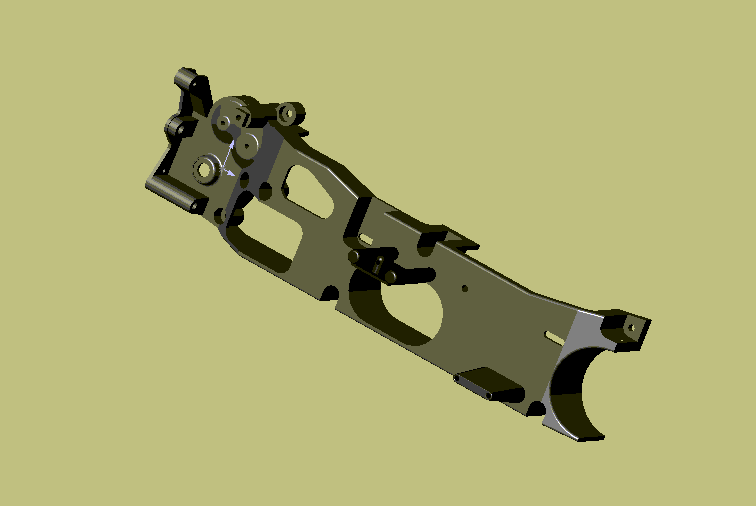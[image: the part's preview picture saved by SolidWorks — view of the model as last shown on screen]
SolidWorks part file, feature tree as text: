
SOLIDWORKS PART (.sldprt)
format: sldprt  version: not decoded by parser v0  size: 1,341,952 bytes
history: native  units: mm
features: sketch x74, cut_extrude x43, extrude x26, fillet x7, plane x6, material x1, shell x1 (+8 scaffold rows collapsed)
feature tree (166):
  scaffold x8  (default folders/planes/origin — collapsed)
  material  "Matériau <non spécifié>"
  plane  "Plane1"
  plane  "Plane2"
  plane  "Plane3"
  sketch  "Esquisse1"  dims[c1.D6=40.0mm c1.D9=6.0mm c1.D4=~4.910474mm c1.D11=28.0mm c1.D13=6.0mm c1.D3=10.0mm c1.D18=10.0mm c1.D19=14.0mm c2.D11=28.0mm c2.D15=14.0mm c3.D11=30.0mm c3.D15=1.0mm c4.D11=22.0mm c4.D21=2.0mm c4.D9=2.0mm c4.D10=3.0mm c5.D9=6.0mm c5.D2=18.0mm c5.D5=6.0mm c5.D6=24.0mm c5.D1=38.0mm c6.D2=~19.312574mm c6.D1=20.0mm c7.D2=38.0mm c7.D3=35.0mm c7.D4=18.0mm c7.D5=18.0mm c7.D7=12.0mm c7.D8=17.0mm c8.D4=23.0mm c8.D6=21.0mm c9.D4=6.0mm c9.D7=14.0mm c9.D8=25.0mm c9.D10=15.0mm c9.D12=16.0mm c9.D14=22.0mm c9.D15=15.0mm c9.D16=23.0mm c9.D17=8.0mm c9.D19=5.0mm c9.D20=30.0mm c9.D21=23.0mm c10.D14=18.0mm c10.D20=23.0mm c10.D21=16.0mm c10.D10=16.0mm c10.D22=14.0mm c10.D1=23.0mm c10.D2=25.0mm c10.D3=15.0mm c10.D4=~1.474586mm c10.D5=20.0mm c10.D6=5.0mm c10.D7=14.0mm c10.D8=16.0mm c11.D5=20.5mm c11.D9=~21.260292mm c11.D8=2.0mm c12.D9=2.0mm c12.D10=2.0mm c12.D11=0.5mm c12.D1=2.0mm]
  sketch  "Esquisse2"  dims[c1.D8=7.0mm c1.D1=18.0mm c1.D2=12.0mm c2.D1=8.0mm c2.D2=4.0mm c2.D3=14.0mm c2.D4=130.0mm c2.D5=22.0mm c2.D6=174.5mm c2.D7=22.0mm]
  sketch  "Esquisse3"  dims[D1=45.0mm D2=12.0mm D3=22.0mm D4=18.0mm D5=15.0mm D6=40.0mm D7=20.0mm D8=35.0mm]
  sketch  "Esquisse4"  dims[D1=5.0mm D2=~135.966117mm]
  sketch  "Esquisse5"  dims[c1.D2=36.0mm c1.D1=34.0mm c1.D5=24.0mm c1.D6=17.0mm c1.D7=12.0mm c1.D10=16.5mm c1.D11=~11.949177mm c2.D1=222.0mm c2.D3=27.0mm c3.D1=217.0mm c3.D3=228.0mm c4.D1=22.8mm c4.D4=19.0mm c5.D1=22.8mm c5.D4=13.0mm c5.D5=14.0mm c5.D6=18.0mm c5.D8=30.0mm c5.D9=2.0mm c5.D2=2.0mm c6.D9=~17.995555mm c6.D6=~17.995555mm c6.D5=19.25mm c7.D6=18.0mm c7.D9=21.0mm]
  sketch  "Esquisse7"  dims[c1.D1=4.0mm c1.D2=2.0mm c1.D3=~18.326793mm c2.D1=194.03mm]
  extrude  "Base-Extrusion"  Depth=27mm
  sketch  "Esquisse8"  dims[c1.D1=12.0mm c1.D2=33.0mm c1.D3=54.0mm c1.D4=159.5mm c1.D5=22.0mm c1.D6=22.0mm c2.D5=5.0mm]
  cut_extrude  "Enlèv. mat.-Extru.1"  Depth=87mm
  sketch  "Esquisse9"
  cut_extrude  "Enlèv. mat.-Extru.2"  [1 undecoded]
  sketch  "Esquisse10"  dims[c1.D1=40.0mm c1.D3=40.0mm c2.D1=40.0mm c2.D2=42.0mm c3.D1=40.0mm c3.D2=53.0mm c4.D1=3.0mm]
  cut_extrude  "Enlèv. mat.-Extru.3"  [1 undecoded]
  sketch  "Esquisse11"  dims[c1.D1=14.0mm c1.D2=20.0mm c1.D4=100.0mm c2.D1=122.0mm c2.D3=2.0mm]
  cut_extrude  "Enlèv. mat.-Extru.8"  [1 undecoded]
  sketch  "Esquisse12"  dims[D4=4.0mm D1=14.0mm D2=21.0mm D3=97.0mm]
  shell  "Coque14"  Thickness=2mm
  sketch  "Esquisse16"  dims[c1.D1=3.0mm c1.D2=3.0mm c2.D1=5.0mm c2.D3=3.0mm c2.D2=3.0mm c2.D5=3.0mm c2.D6=5.0mm c3.D2=8.0mm c3.D3=6.0mm c3.D4=32.0mm]
  cut_extrude  "Enlèv. mat.-Extru.11"  [1 undecoded]
  sketch  "Esquisse17"  dims[c1.D3=4.0mm c1.D1=1.5mm c1.D2=1.5mm c2.D3=~0.877384mm]
  extrude  "Boss.-Extru.8"  Depth=13.5mm
  cut_extrude  "Enlèv. mat.-Extru.12"  Depth=12mm
  sketch  "Esquisse18"  dims[D1=18.0mm D2=3.0mm D3=8.0mm]
  cut_extrude  "Enlèv. mat.-Extru.13"  [1 undecoded]
  sketch  "Esquisse19"  dims[c1.D6=40.0mm c1.D9=6.0mm c1.D4=~4.910474mm c1.D11=28.0mm c1.D13=6.0mm c1.D3=10.0mm c1.D18=10.0mm c1.D19=14.0mm c2.D11=28.0mm c2.D15=14.0mm c3.D11=30.0mm c3.D15=1.0mm c4.D11=22.0mm c4.D21=2.0mm c4.D9=2.0mm c4.D10=3.0mm c5.D9=6.0mm c5.D2=18.0mm c5.D5=6.0mm c5.D6=24.0mm c5.D4=12.0mm c5.D1=20.0mm c6.D2=38.0mm c6.D3=35.0mm c6.D4=18.0mm c6.D5=18.0mm c6.D7=12.0mm c6.D8=17.0mm c7.D4=23.0mm c7.D6=21.0mm c8.D4=6.0mm c8.D7=14.0mm c8.D8=25.0mm c8.D10=15.0mm c8.D12=16.0mm c8.D14=22.0mm c8.D15=15.0mm c8.D16=23.0mm c8.D17=8.0mm c8.D19=5.0mm c8.D20=30.0mm c8.D21=23.0mm c9.D14=18.0mm c9.D20=23.0mm c9.D21=16.0mm c9.D10=16.0mm c9.D22=14.0mm c9.D1=23.0mm c9.D2=25.0mm c9.D3=15.0mm c9.D4=~1.474586mm c9.D5=20.0mm c9.D6=5.0mm c9.D7=14.0mm c9.D8=16.0mm c10.D5=20.5mm c10.D9=~21.260292mm c10.D8=2.0mm c11.D9=2.0mm c11.D10=2.0mm c11.D11=0.5mm c11.D1=2.0mm c11.D2=15.2mm c11.D3=23.2mm c11.D5=~34.247688mm c11.D6=19.25mm]
  extrude  "Boss.-Extru.9"  [1 undecoded]
  sketch  "Esquisse20"
  cut_extrude  "Enlèv. mat.-Extru.14"  [1 undecoded]
  sketch  "Esquisse21"  dims[D1=27.0mm]
  extrude  "Boss.-Extru.10"  Depth=8mm
  sketch  "Esquisse22"
  sketch  "Esquisse24"  dims[D1=2.0mm D2=2.0mm]
  sketch  "Esquisse25"
  extrude  "Boss.-Extru.12"  Depth=8mm
  cut_extrude  "Enlèv. mat.-Extru.17"  Depth=6mm
  sketch  "Esquisse26"
  cut_extrude  "Enlèv. mat.-Extru.18"  Depth=6mm
  sketch  "Esquisse27"  dims[D1=5.0mm D2=9.0mm D3=9.0mm D4=5.0mm]
  sketch  "Esquisse29"  dims[D1=13.0mm]
  extrude  "Boss.-Extru.14"  Depth=4mm
  sketch  "Esquisse30"  dims[D1=11.0mm]
  cut_extrude  "Enlèv. mat.-Extru.19"  Depth=4mm
  sketch  "Esquisse31"  dims[D1=6.0mm]
  cut_extrude  "Enlèv. mat.-Extru.20"  [1 undecoded]
  sketch  "Esquisse32"  dims[D1=10.0mm]
  cut_extrude  "Enlèv. mat.-Extru.21"  Depth=0.5mm
  fillet  "Congé1"  Radius=1mm
  cut_extrude  "Enlèv. mat.-Extru.22"  [1 undecoded]
  sketch  "Esquisse33"  dims[c1.D5=8.0mm c1.D6=2.0mm c1.D4=3.5mm c1.D9=4.5mm c1.D13=2.0mm c1.D16=2.0mm c1.D20=4.0mm c1.D1=27.0mm c1.D2=23.0mm c1.D3=23.0mm c2.D4=32.0mm c2.D1=~1.086371mm c2.D2=~4.577798mm c2.D3=~6.268805mm c2.D5=~20.368425mm c2.D6=~22.368425mm c2.D7=~5.486411mm c2.D8=~3.722962mm c2.D10=~4.480709mm c2.D11=~2.79739mm c2.D12=~1.991426mm c2.D14=~8.25742mm c2.D15=~7.451456mm c2.D17=~1.864614mm c2.D18=~2.575873mm c2.D19=~3.829958mm c2.D21=~3.95603mm c2.D22=~0.95603mm c2.D23=~19.561627mm c2.D24=~8.593709mm c2.D25=~10.24482mm c2.D26=7.0mm c2.D27=7.0mm c2.D28=~14.527757mm c2.D29=~14.406696mm c2.D30=~22.153872mm c2.D31=12.0mm c2.D32=12.0mm c2.D33=38.0mm]
  extrude  "Boss.-Extru.16"  Depth=1.5mm
  sketch  "Esquisse35"
  extrude  "Boss.-Extru.17"  Depth=22.5mm
  sketch  "Esquisse36"  dims[D1=8.0mm]
  extrude  "Boss.-Extru.18"  Depth=4mm
  sketch  "Esquisse37"  dims[c1.D6=4.0mm c1.D1=~8.352254mm c1.D2=~4.379415mm c1.D3=~3.829958mm c1.D4=~1.153872mm c1.D5=~0.436764mm c2.D6=~9.881926mm c2.D7=~10.474589mm c2.D8=16.56mm c2.D9=21.0mm]
  extrude  "Boss.-Extru.19"  Depth=5mm
  sketch  "Esquisse38"  dims[D1=~4.01424mm]
  extrude  "Boss.-Extru.20"  Depth=1.5mm
  sketch  "Esquisse39"  dims[D1=2.0mm D2=4.0mm D3=3.0mm]
  cut_extrude  "Enlèv. mat.-Extru.23"  [1 undecoded]
  fillet  "Congé2"  Radius=1mm
  fillet  "Congé3"  Radius=1mm
  sketch  "Esquisse42"  dims[c1.D4=5.0mm c1.D8=3.0mm c1.D3=3.0mm c1.D6=3.0mm c1.D11=5.0mm c1.D12=5.0mm c2.D8=5.0mm c2.D1=14.0mm c2.D2=32.0mm c2.D3=75.0mm c2.D5=20.0mm c2.D6=72.0mm c2.D7=22.0mm c3.D1=19.0mm c3.D2=66.0mm c3.D4=72.0mm c3.D5=19.0mm c3.D7=20.0mm c3.D8=14.0mm c3.D9=9.0mm c3.D10=65.0mm c3.D13=9.0mm c4.D13=90.0deg c5.D13=9.0mm c5.D14=75.0mm c5.D15=19.84mm c5.D16=27.02mm c5.D9=9.0mm c6.D9=90.0deg c7.D9=8.0mm c7.D10=8.0mm]
  cut_extrude  "Enlèv. mat.-Extru.24"  Depth=20mm
  sketch  "Esquisse43"
  cut_extrude  "Enlèv. mat.-Extru.25"  Depth=10mm
  sketch  "Esquisse46"  dims[D2=10.0mm D1=45.0mm]
  extrude  "Boss.-Extru.23"  Depth=14mm
  sketch  "Esquisse48"  dims[D1=8.0mm]
  cut_extrude  "Enlèv. mat.-Extru.27"  Depth=13mm
  sketch  "Esquisse49"  dims[D1=3.0mm]
  cut_extrude  "Enlèv. mat.-Extru.28"  [1 undecoded]
  sketch  "Esquisse50"  dims[D1=5.0mm]
  cut_extrude  "Enlèv. mat.-Extru.29"  [1 undecoded]
  sketch  "Esquisse51"  dims[c1.D2=10.0mm c1.D1=5.0mm c1.D3=10.0mm c2.D1=5.0mm]
  extrude  "Boss.-Extru.24"  [1 undecoded]
  sketch  "Esquisse54"  dims[D1=3.0mm]
  cut_extrude  "Enlèv. mat.-Extru.32"  [1 undecoded]
  sketch  "Esquisse55"  dims[D1=7.0mm]
  cut_extrude  "Enlèv. mat.-Extru.33"  Depth=4mm
  plane  "Plan1"  Offset=8mm
  sketch  "Esquisse57"
  cut_extrude  "Enlèv. mat.-Extru.35"  [1 undecoded]
  sketch  "Esquisse58"  dims[D1=3.0mm]
  cut_extrude  "Enlèv. mat.-Extru.36"  [1 undecoded]
  sketch  "Esquisse59"  dims[D1=7.0mm]
  cut_extrude  "Enlèv. mat.-Extru.37"  Depth=4mm
  sketch  "Esquisse60"  dims[D1=7.0mm]
  cut_extrude  "Enlèv. mat.-Extru.38"  Depth=3mm
  fillet  "Congé4"  Radius=1mm
  sketch  "Esquisse61"  dims[D1=10.0mm D2=17.0mm D3=16.6mm]
  cut_extrude  "Enlèv. mat.-Extru.39"  Depth=10mm
  plane  "Plan2"  Offset=11mm
  sketch  "Esquisse64"
  extrude  "Boss.-Extru.29"  [1 undecoded]
  sketch  "Esquisse65"
  cut_extrude  "Enlèv. mat.-Extru.40"  Depth=5mm
  extrude  "Boss.-Extru.30"  Depth=6mm
  sketch  "Esquisse66"
  extrude  "Boss.-Extru.31"  Depth=10mm
  sketch  "Esquisse67"
  extrude  "Boss.-Extru.32"  [1 undecoded]
  sketch  "Esquisse68"  dims[c1.D1=10.0mm c1.D2=~4.410927mm c1.D3=~4.410927mm c1.D4=10.0mm c2.D1=~37.209373mm c2.D2=5.0mm c2.D3=78.0mm c2.D5=33.0mm]
  extrude  "Boss.-Extru.33"  [1 undecoded]
  sketch  "Esquisse69"  dims[c1.D1=7.0mm c1.D2=7.0mm c2.D1=5.0mm]
  cut_extrude  "Enlèv. mat.-Extru.41"  Depth=4mm
  sketch  "Esquisse70"  dims[D1=8.0mm D2=8.0mm D3=8.0mm]
  cut_extrude  "Enlèv. mat.-Extru.44"  Depth=22mm
  sketch  "Esquisse71"  dims[D1=3.0mm D2=3.0mm]
  cut_extrude  "Enlèv. mat.-Extru.45"  [1 undecoded]
  sketch  "Esquisse72"  dims[D1=6.0mm D2=6.0mm D3=3.0mm D4=3.0mm]
  extrude  "Boss.-Extru.34"  Depth=3mm
  sketch  "Esquisse73"  dims[D1=2.5mm]
  cut_extrude  "Enlèv. mat.-Extru.46"  Depth=10mm
  sketch  "Esquisse74"  dims[D3=6.0mm D1=10.0mm D2=18.0mm]
  extrude  "Boss.-Extru.35"  Depth=32mm
  sketch  "Esquisse75"
  extrude  "Boss.-Extru.36"  Depth=1mm
  fillet  "Congé6"  Radius=1mm
  sketch  "Esquisse76"  dims[D2=4.0mm D1=10.0mm D3=5.0mm]
  extrude  "Boss.-Extru.37"  Depth=8mm
  fillet  "Congé9"  Radius=2mm
  sketch  "Esquisse77"  dims[D2=2.0mm D1=10.0mm D3=6.0mm]
  cut_extrude  "Enlèv. mat.-Extru.47"  Depth=18mm
  sketch  "Esquisse78"  dims[c1.D2=3.0mm c1.D3=3.0mm c1.D4=3.0mm c1.D8=3.0mm c1.D9=3.0mm c1.D1=12.0mm c1.D5=8.0mm c1.D6=44.0mm c1.D7=22.0mm c2.D4=7.0mm c2.D10=16.5mm c2.D11=30.0mm]
  cut_extrude  "Enlèv. mat.-Extru.48"  [1 undecoded]
  sketch  "Esquisse79"  dims[D3=10.0mm D1=93.75mm D2=7.25mm]
  extrude  "Boss.-Extru.38"  Depth=40mm
  sketch  "Esquisse80"
  cut_extrude  "Enlèv. mat.-Extru.49"  Depth=40mm
  sketch  "Esquisse81"  dims[D1=8.0mm]
  cut_extrude  "Enlèv. mat.-Extru.50"  Depth=22mm
  sketch  "Esquisse82"  dims[D1=7.0mm]
  cut_extrude  "Enlèv. mat.-Extru.51"  Depth=2mm
  sketch  "Esquisse83"  dims[D1=3.0mm]
  cut_extrude  "Enlèv. mat.-Extru.52"  [1 undecoded]
  sketch  "Esquisse84"
  cut_extrude  "Enlèv. mat.-Extru.54"  Depth=10mm
  sketch  "Esquisse85"  dims[D1=9.0mm D2=9.0mm]
  extrude  "Boss.-Extru.41"  [1 undecoded]
  sketch  "Esquisse86"  dims[D1=9.0mm]
  extrude  "Boss.-Extru.42"  [1 undecoded]
  sketch  "Esquisse87"  dims[D1=6.0mm D2=6.0mm]
  cut_extrude  "Enlèv. mat.-Extru.55"  Depth=3mm
  sketch  "Esquisse88"  dims[D1=3.0mm D2=3.0mm]
  cut_extrude  "Enlèv. mat.-Extru.56"  [1 undecoded]
  plane  "Plan3"  Offset=3mm
  sketch  "Esquisse89"  dims[D1=7.0mm D2=7.0mm]
  cut_extrude  "Enlèv. mat.-Extru.57"  [1 undecoded]
  sketch  "Esquisse90"  dims[D2=8.0mm D3=8.0mm D1=7.0mm D4=17.0mm D5=32.5mm]
  extrude  "Boss.-Extru.43"  Depth=24mm
  sketch  "Esquisse91"  dims[D1=2.0mm D2=2.0mm]
  cut_extrude  "Enlèv. mat.-Extru.58"  Depth=10mm
  fillet  "Congé12"  Radius=0.4mm
decode coverage: 110 of 151 modeling features carry decoded parameters
note: ~ marks probable driven/reference dimensions
note: 26 parameter values undecoded
summary: no parameter record found for 26 features
note: suppression state not decoded; provenance and decode notes live in map.json
